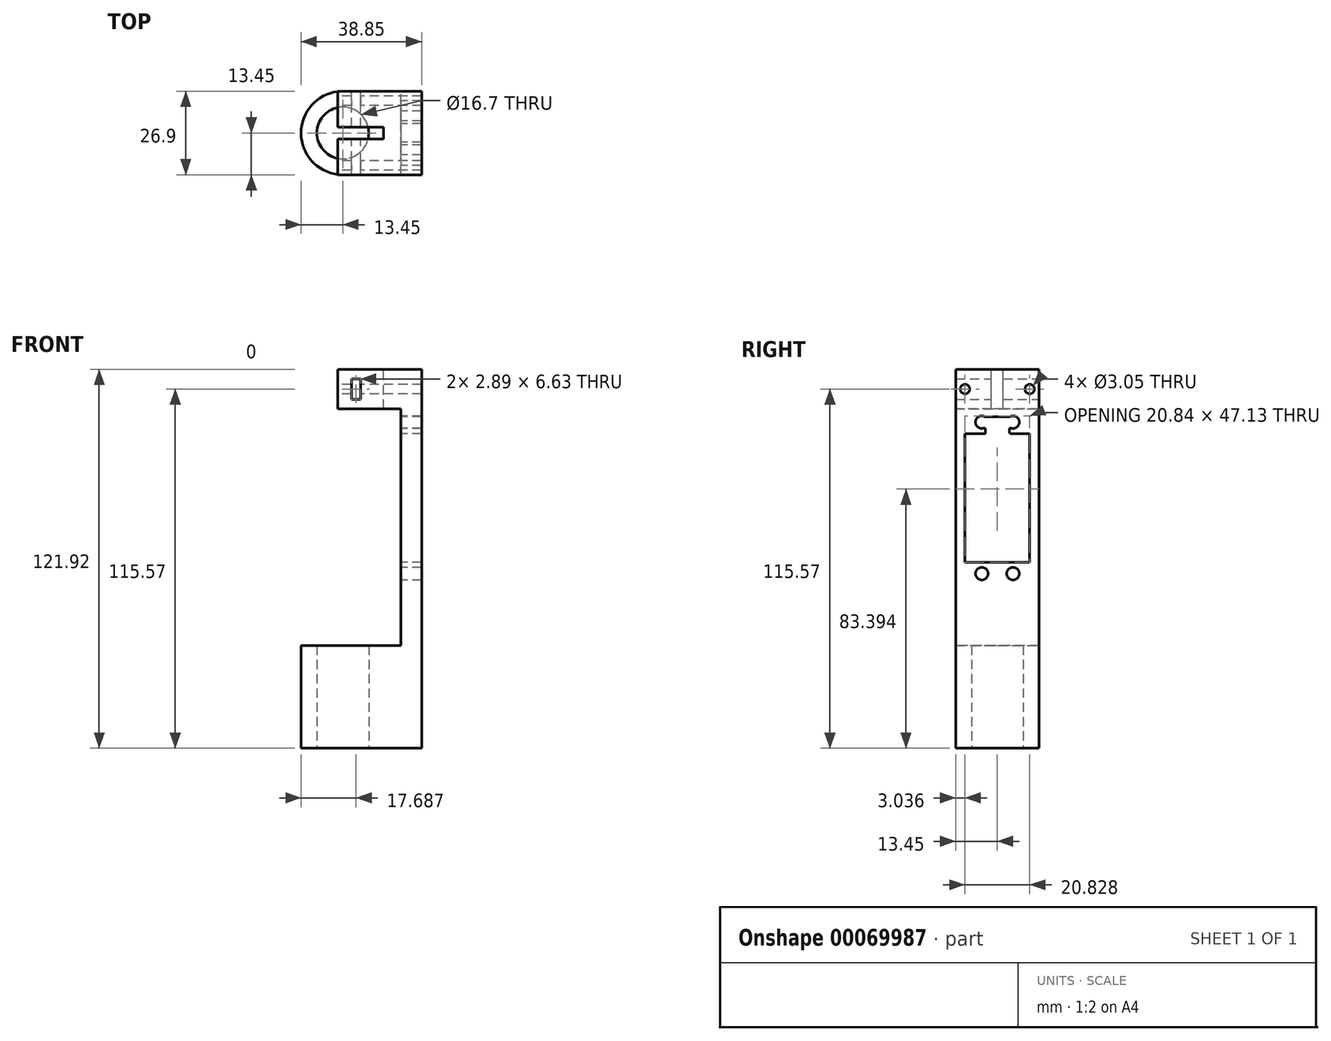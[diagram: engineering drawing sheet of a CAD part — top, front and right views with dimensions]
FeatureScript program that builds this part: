
annotation { "Feature Type Name" : "Feature", "Feature Type Description" : "" }
export const myFeature = defineFeature(function(context is Context, id is Id, definition is map)
    precondition{}
    {
        {
            var Q0;
            Q0=qCreatedBy(makeId("Top.planeOp"),FACE);
            var sketch = newSketch(context, id + "F0", { "sketchPlane" : qUnion([Q0])});
            skCircle(sketch, "E0", {"center": v(0, 0) * mm, "radius": 8.35 * mm});
            skArc(sketch, "E1", {"start": v(0, 13.45) * mm, "mid": v(-13.45, 0) * mm, "end": v(0, -13.45) * mm});
            skLineSegment(sketch, "E2", {"start": v(0, 13.45) * mm, "end": v(25.4, 13.45) * mm});
            skLineSegment(sketch, "E3", {"start": v(25.4, 13.45) * mm, "end": v(25.4, -13.45) * mm});
            skLineSegment(sketch, "E4", {"start": v(25.4, -13.45) * mm, "end": v(0, -13.45) * mm});
            skSolve(sketch);
        }
        {
            var Q0;
            Q0 = qSketchRegion(id + "F0", true);
            extrude(context, id + "F1", {"entities" : qUnion([Q0]), "depth" : 33.02 * mm});
        }
        {
            var Q0;
            Q0=makeQuery(id+"F1.opExtrude","CAP_FACE",FACE,{"disambiguationData":[OSD([sQuery(id+"F0.wireOp",EDGE,"E0"),sQuery(id+"F0.wireOp",EDGE,"E1"),sQuery(id+"F0.wireOp",EDGE,"E2"),sQuery(id+"F0.wireOp",EDGE,"E3"),sQuery(id+"F0.wireOp",EDGE,"E4")])],"isStart":false});
            var sketch = newSketch(context, id + "F2", { "sketchPlane" : qUnion([Q0])});
            skLineSegment(sketch, "E5.bottom", {"start": v(25.4, -13.45) * mm, "end": v(18.7, -13.45) * mm});
            skLineSegment(sketch, "E5.top", {"start": v(25.4, 13.45) * mm, "end": v(18.7, 13.45) * mm});
            skLineSegment(sketch, "E5.left", {"start": v(25.4, -13.45) * mm, "end": v(25.4, 13.45) * mm});
            skLineSegment(sketch, "E5.right", {"start": v(18.7, -13.45) * mm, "end": v(18.7, 13.45) * mm});
            skSolve(sketch);
        }
        {
            var Q0;
            Q0 = qSketchRegion(id + "F2", true);
            extrude(context, id + "F3", {"entities" : qUnion([Q0]), "operationType" : NewBodyOperationType.ADD, "depth" : 76.2 * mm});
        }
        {
            var Q0;
            Q0=makeQuery(id+"F3.opExtrude","SWEPT_FACE",FACE,{"disambiguationData":[OSD([sQuery(id+"F2.wireOp",EDGE,"E5.right")])]});
            var sketch = newSketch(context, id + "F4", { "sketchPlane" : qUnion([Q0])});
            skLineSegment(sketch, "E6.bottom", {"start": v(-10.42, 101.27) * mm, "end": v(10.42, 101.27) * mm});
            skLineSegment(sketch, "E6.top", {"start": v(-10.42, 59.83) * mm, "end": v(10.42, 59.83) * mm});
            skLineSegment(sketch, "E6.left", {"start": v(-10.42, 101.27) * mm, "end": v(-10.42, 59.83) * mm});
            skLineSegment(sketch, "E6.right", {"start": v(10.42, 101.27) * mm, "end": v(10.42, 59.83) * mm});
            skLineSegment(sketch, "E7", {"start": v(-10.42, 80.55) * mm, "end": v(10.42, 80.55) * mm, "construction": true});
            skLineSegment(sketch, "E8", {"start": v(0, 59.83) * mm, "end": v(0, 101.27) * mm, "construction": true});
            skCircle(sketch, "E9", {"center": v(-5.02, 104.93) * mm, "radius": 2.03 * mm});
            skLineSegment(sketch, "E10", {"start": v(0, 33.02) * mm, "end": v(0, 109.22) * mm, "construction": true});
            skCircle(sketch, "E11.MirrorC", {"center": v(-5.02, 56.17) * mm, "radius": 2.03 * mm});
            skCircle(sketch, "E12.MirrorC", {"center": v(5.02, 56.17) * mm, "radius": 2.03 * mm});
            skCircle(sketch, "E13.MirrorC", {"center": v(5.02, 104.93) * mm, "radius": 2.03 * mm});
            skSolve(sketch);
        }
        {
            var Q0;
            Q0 = qSketchRegion(id + "F4", true);
            extrude(context, id + "F5", {"entities" : qUnion([Q0]), "operationType" : NewBodyOperationType.REMOVE, "oppositeDirection" : true, "depth" : 25.4 * mm});
        }
        {
            var Q0;
            Q0=makeQuery(id+"F3.opExtrude","SWEPT_FACE",FACE,{"disambiguationData":[OSD([sQuery(id+"F2.wireOp",EDGE,"E5.right")])]});
            var sketch = newSketch(context, id + "F6", { "sketchPlane" : qUnion([Q0])});
            skLineSegment(sketch, "E14", {"start": v(0, 109.22) * mm, "end": v(0, 101.27) * mm, "construction": true});
            skLineSegment(sketch, "E15.bottom", {"start": v(-3.88, 101.27) * mm, "end": v(3.88, 101.27) * mm});
            skLineSegment(sketch, "E15.top", {"start": v(-3.88, 106.62) * mm, "end": v(3.88, 106.62) * mm});
            skLineSegment(sketch, "E15.left", {"start": v(-3.88, 101.27) * mm, "end": v(-3.88, 106.62) * mm});
            skLineSegment(sketch, "E15.right", {"start": v(3.88, 101.27) * mm, "end": v(3.88, 106.62) * mm});
            skLineSegment(sketch, "E16", {"start": v(0, 106.62) * mm, "end": v(0, 101.27) * mm, "construction": true});
            skSolve(sketch);
        }
        {
            var Q0;
            Q0 = qSketchRegion(id + "F6", true);
            extrude(context, id + "F7", {"entities" : qUnion([Q0]), "operationType" : NewBodyOperationType.REMOVE, "oppositeDirection" : true, "depth" : 25.4 * mm});
        }
        {
            var Q0;
            Q0=makeQuery(id+"F7.boolean.opBoolean","INTERSECT",EDGE,{"derivedFrom":[makeQuery(id+"F5.boolean.opBoolean","COPY",FACE,{"derivedFrom":makeQuery(id+"F5.opExtrude","SWEPT_FACE",FACE,{"disambiguationData":[OSD([sQuery(id+"F4.wireOp",EDGE,"E9")])]})}),makeQuery(id+"F7.opExtrude","SWEPT_FACE",FACE,{"disambiguationData":[OSD([sQuery(id+"F6.wireOp",EDGE,"E15.left")])]})]});
            var Q1;
            Q1=makeQuery(id+"F7.boolean.opBoolean","INTERSECT",EDGE,{"derivedFrom":[makeQuery(id+"F5.boolean.opBoolean","COPY",FACE,{"derivedFrom":makeQuery(id+"F5.opExtrude","SWEPT_FACE",FACE,{"disambiguationData":[OSD([sQuery(id+"F4.wireOp",EDGE,"E13.MirrorC")])]})}),makeQuery(id+"F7.opExtrude","SWEPT_FACE",FACE,{"disambiguationData":[OSD([sQuery(id+"F6.wireOp",EDGE,"E15.right")])]})]});
            var Q2;
            Q2=makeQuery(id+"F7.boolean.opBoolean","COPY",EDGE,{"derivedFrom":makeQuery(id+"F7.opExtrude","SWEPT_EDGE",EDGE,{"disambiguationData":[OSD([sQuery(id+"F4.wireOp",EDGE,"E6.bottom"),sQuery(id+"F6.wireOp",EDGE,"E15.bottom"),sQuery(id+"F6.wireOp",EDGE,"E15.left")])]})});
            var Q3;
            Q3=makeQuery(id+"F7.boolean.opBoolean","COPY",EDGE,{"derivedFrom":makeQuery(id+"F7.opExtrude","SWEPT_EDGE",EDGE,{"disambiguationData":[OSD([sQuery(id+"F4.wireOp",EDGE,"E6.bottom"),sQuery(id+"F6.wireOp",EDGE,"E15.bottom"),sQuery(id+"F6.wireOp",EDGE,"E15.right")])]})});
            var Q4;
            Q4=makeQuery(id+"F7.boolean.opBoolean","COPY",EDGE,{"derivedFrom":makeQuery(id+"F7.opExtrude","SWEPT_EDGE",EDGE,{"disambiguationData":[OSD([sQuery(id+"F4.wireOp",EDGE,"E9"),sQuery(id+"F6.wireOp",EDGE,"E15.top"),sQuery(id+"F6.wireOp",EDGE,"E15.left")])]})});
            var Q5;
            Q5=makeQuery(id+"F7.boolean.opBoolean","COPY",EDGE,{"derivedFrom":makeQuery(id+"F7.opExtrude","SWEPT_EDGE",EDGE,{"disambiguationData":[OSD([sQuery(id+"F4.wireOp",EDGE,"E13.MirrorC"),sQuery(id+"F6.wireOp",EDGE,"E15.top"),sQuery(id+"F6.wireOp",EDGE,"E15.right")])]})});
            fillet(context, id + "F8", {"entities" : qUnion([Q0, Q1, Q2, Q3, Q4, Q5]), "radius" : .4 * mm, "tangentPropagation" : true, "allowEdgeOverflow" : false});
        }
        {
            var Q0;
            Q0=makeQuery(id+"F3.opExtrude","CAP_FACE",FACE,{"disambiguationData":[OSD([sQuery(id+"F2.wireOp",EDGE,"E5.bottom"),sQuery(id+"F2.wireOp",EDGE,"E5.top"),sQuery(id+"F2.wireOp",EDGE,"E5.left"),sQuery(id+"F2.wireOp",EDGE,"E5.right")])],"isStart":false});
            var sketch = newSketch(context, id + "F9", { "sketchPlane" : qUnion([Q0])});
            skLineSegment(sketch, "E17.bottom", {"start": v(25.4, 13.45) * mm, "end": v(-1.65, 13.45) * mm});
            skLineSegment(sketch, "E17.top", {"start": v(25.4, -13.45) * mm, "end": v(-1.65, -13.45) * mm});
            skLineSegment(sketch, "E17.left", {"start": v(25.4, 13.45) * mm, "end": v(25.4, -13.45) * mm});
            skLineSegment(sketch, "E17.right", {"start": v(-1.65, 13.45) * mm, "end": v(-1.65, -13.45) * mm});
            skSolve(sketch);
        }
        {
            var Q0;
            Q0 = qSketchRegion(id + "F9", true);
            extrude(context, id + "F10", {"entities" : qUnion([Q0]), "operationType" : NewBodyOperationType.ADD, "depth" : 12.7 * mm});
        }
        {
            var Q0;
            Q0=makeQuery(id+"F10.opExtrude","SWEPT_FACE",FACE,{"disambiguationData":[OSD([sQuery(id+"F9.wireOp",EDGE,"E17.right")])]});
            var sketch = newSketch(context, id + "F11", { "sketchPlane" : qUnion([Q0])});
            skLineSegment(sketch, "E18", {"start": v(0, 121.92) * mm, "end": v(0, 109.22) * mm, "construction": true});
            skLineSegment(sketch, "E19.bottom", {"start": v(-1.9, 109.22) * mm, "end": v(1.9, 109.22) * mm});
            skLineSegment(sketch, "E19.top", {"start": v(-1.9, 121.92) * mm, "end": v(1.9, 121.92) * mm});
            skLineSegment(sketch, "E19.left", {"start": v(-1.9, 109.22) * mm, "end": v(-1.9, 121.92) * mm});
            skLineSegment(sketch, "E19.right", {"start": v(1.9, 109.22) * mm, "end": v(1.9, 121.92) * mm});
            skPoint(sketch, "E20", {"position": v(0, 121.92) * mm});
            skLineSegment(sketch, "E21", {"start": v(-13.45, 115.57) * mm, "end": v(13.45, 115.57) * mm, "construction": true});
            skCircle(sketch, "E22", {"center": v(-10.41, 115.57) * mm, "radius": 1.52 * mm});
            skCircle(sketch, "E23.MirrorC", {"center": v(10.41, 115.57) * mm, "radius": 1.52 * mm});
            skSolve(sketch);
        }
        {
            var Q0;
            Q0 = qSketchRegion(id + "F11", true);
            extrude(context, id + "F12", {"entities" : qUnion([Q0]), "operationType" : NewBodyOperationType.REMOVE, "oppositeDirection" : true, "depth" : 7.4 * mm * 2});
        }
        {
            var Q0;
            Q0=makeQuery(id+"F12.boolean.opBoolean","COPY",FACE,{"derivedFrom":makeQuery(id+"F12.opExtrude","CAP_FACE",FACE,{"disambiguationData":[OSD([sQuery(id+"F11.wireOp",EDGE,"E22")])],"isStart":false})});
            var Q1;
            Q1=makeQuery(id+"F12.boolean.opBoolean","COPY",FACE,{"derivedFrom":makeQuery(id+"F12.opExtrude","CAP_FACE",FACE,{"disambiguationData":[OSD([sQuery(id+"F11.wireOp",EDGE,"E23.MirrorC")])],"isStart":false})});
            extrude(context, id + "F13", {"entities" : qUnion([Q0, Q1]), "operationType" : NewBodyOperationType.REMOVE, "oppositeDirection" : true, "depth" : 12.7 * mm});
        }
        {
            var Q0;
            Q0=makeQuery(id+"F10.boolean.opBoolean","MERGE",FACE,{"derivedFrom":[makeQuery(id+"F3.boolean.opBoolean","MERGE",FACE,{"derivedFrom":[makeQuery(id+"F1.opExtrude","SWEPT_FACE",FACE,{"disambiguationData":[OSD([sQuery(id+"F0.wireOp",EDGE,"E2")])]}),makeQuery(id+"F3.opExtrude","SWEPT_FACE",FACE,{"disambiguationData":[OSD([sQuery(id+"F2.wireOp",EDGE,"E5.top")])]})]}),makeQuery(id+"F10.opExtrude","SWEPT_FACE",FACE,{"disambiguationData":[OSD([sQuery(id+"F9.wireOp",EDGE,"E17.bottom")])]})]});
            var sketch = newSketch(context, id + "F14", { "sketchPlane" : qUnion([Q0])});
            skLineSegment(sketch, "E24.bottom", {"start": v(-2.8, 118.88) * mm, "end": v(-5.68, 118.88) * mm});
            skLineSegment(sketch, "E24.top", {"start": v(-2.8, 112.26) * mm, "end": v(-5.68, 112.26) * mm});
            skLineSegment(sketch, "E24.left", {"start": v(-2.8, 118.88) * mm, "end": v(-2.8, 112.26) * mm});
            skLineSegment(sketch, "E24.right", {"start": v(-5.68, 118.88) * mm, "end": v(-5.68, 112.26) * mm});
            skLineSegment(sketch, "E25", {"start": v(1.65, 115.57) * mm, "end": v(-25.4, 115.57) * mm, "construction": true});
            skPoint(sketch, "E26", {"position": v(-2.8, 115.57) * mm});
            skSolve(sketch);
        }
        {
            var Q0;
            Q0 = qSketchRegion(id + "F14", true);
            extrude(context, id + "F15", {"entities" : qUnion([Q0]), "operationType" : NewBodyOperationType.REMOVE, "endBound" : BoundingType.THROUGH_ALL, "oppositeDirection" : true, "depth" : 25.4 * mm});
        }
    });
